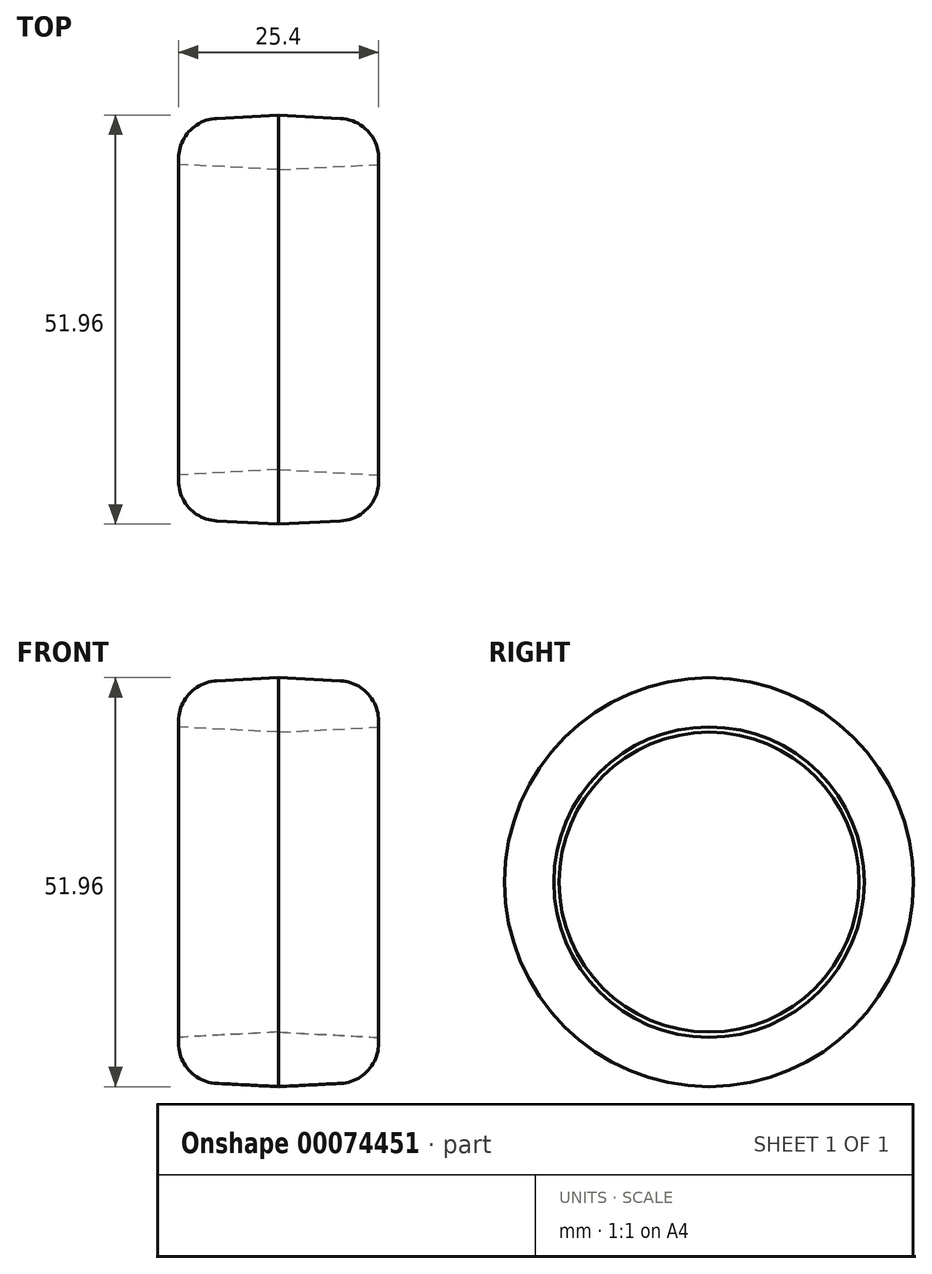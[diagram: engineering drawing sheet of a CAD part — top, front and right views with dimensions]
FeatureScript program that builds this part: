
annotation { "Feature Type Name" : "Feature", "Feature Type Description" : "" }
export const myFeature = defineFeature(function(context is Context, id is Id, definition is map)
    precondition{}
    {
        {
            var Q0;
            Q0=qCreatedBy(makeId("Top.planeOp"),FACE);
            var sketch = newSketch(context, id + "F0", { "sketchPlane" : qUnion([Q0])});
            skLineSegment(sketch, "E0", {"start": v(0, -4.02) * mm, "end": v(0, 126.4) * mm});
            skSolve(sketch);
        }
        {
            var Q0;
            Q0=qCreatedBy(makeId("Right.planeOp"),FACE);
            cPlane(context, id + "F1", {"entities" : qUnion([Q0]), "cplaneType" : CPlaneType.OFFSET, "offset" : 50.8 * mm, "width" : 152.4 * mm, "height" : 152.4 * mm});
        }
        {
            var Q0;
            Q0=qCreatedBy(id+"F1.planeOp",FACE);
            var sketch = newSketch(context, id + "F2", { "sketchPlane" : qUnion([Q0])});
            skCircle(sketch, "E1", {"center": v(0, 0) * mm, "radius": 25.98 * mm});
            skCircle(sketch, "E2", {"center": v(0, 0) * mm, "radius": 19.05 * mm});
            skSolve(sketch);
        }
        {
            var Q0;
            Q0=makeQuery(id+"F2.imprint","IMPRINT",FACE,{"disambiguationData":[TD([[makeQuery(id+"F2.imprint","IMPRINT",EDGE,{"derivedFrom":sQuery(id+"F2.wireOp",EDGE,"E1")}),1.0]])]});
            extrude(context, id + "F3", {"entities" : qUnion([Q0]), "endBound" : BoundingType.SYMMETRIC, "depth" : 25.4 * mm, "hasDraft" : true, "draftAngle" : 3 * degree, "draftPullDirection" : true});
        }
        {
            var Q0;
            Q0=makeQuery(id+"F3.opExtrude","CAP_EDGE",EDGE,{"disambiguationData":[OSD([sQuery(id+"F2.wireOp",EDGE,"E1")])],"isStart":false});
            fillet(context, id + "F4", {"entities" : qUnion([Q0]), "radius" : 5.08 * mm, "tangentPropagation" : true, "allowEdgeOverflow" : false});
        }
        {
            var Q0;
            Q0=makeQuery(id+"F3.opExtrude","CAP_EDGE",EDGE,{"disambiguationData":[OSD([sQuery(id+"F2.wireOp",EDGE,"E1")])],"isStart":true});
            fillet(context, id + "F5", {"entities" : qUnion([Q0]), "radius" : 5.08 * mm, "tangentPropagation" : true, "allowEdgeOverflow" : false});
        }
    });
